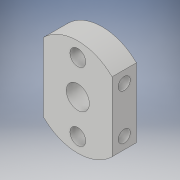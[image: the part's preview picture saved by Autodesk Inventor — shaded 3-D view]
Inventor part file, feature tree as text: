
AUTODESK INVENTOR PART (.ipt)
format: ipt  version: 2019 (Build 230136000, 136)  size: 145,408 bytes
history: native  units: in
note: dims shown in document units (in); Inventor stores cm internally (conversion verified against a paired STEP export)
features: sketch x5, hole x3, extrude x2, plane x1, mirror x1, projected_geometry x1
ambient origin geometry x8: Origin, YZ Plane, XZ Plane, XY Plane, X Axis, Y Axis, Z Axis, Center Point
bodies: Solid1 (feature_tree)
feature tree (13):
  extrude  "Extrusion1"  Depth=0.4in TaperAngle=0.0deg
  hole  "Hole1"  [1 undecoded]
  hole  "Hole2"  [1 undecoded]
  extrude  "Extrusion2"  Depth=0.4in TaperAngle=0.0deg
  hole  "Hole3"  [1 undecoded]
  plane  "Work Plane1"
  mirror  "Mirror1"
  sketch  "Sketch1"  dims[d0=1.6in d1=0.4in d2=0.0in]
  sketch  "Sketch2"  dims[d3=0.38in d4=0.276in d5=0.438in d6=0.25in d7=0.5635in d8=0.432in d9=0.8108in d10=1.125in]
  sketch  "Sketch3"  dims[d11=0.5625in]
  sketch  "Sketch4"  dims[d12=0.26in d13=0.276in d14=0.281in d15=0.138in d16=0.5635in d17=0.432in d18=0.8108in d19=1.125in]
  sketch  "Sketch5"  dims[d20=0.5625in d21=0.4in d22=0.0in d23=0.4in d24=0.2in d25=0.2in d26=0.75in d27=1.1377in d28=0.1939in d29=0.2in d30=0.75in d31=0.375in d32=0.25in d33=0.5635in d34=0.432in d35=0.8108in]
  projected_geometry  "Projected Loop1"
note: 3 required parameter values undecoded (feature->parameter linkage not recoverable at this tier; creation-order binding heuristic only, values carry confidence <= 0.55)
